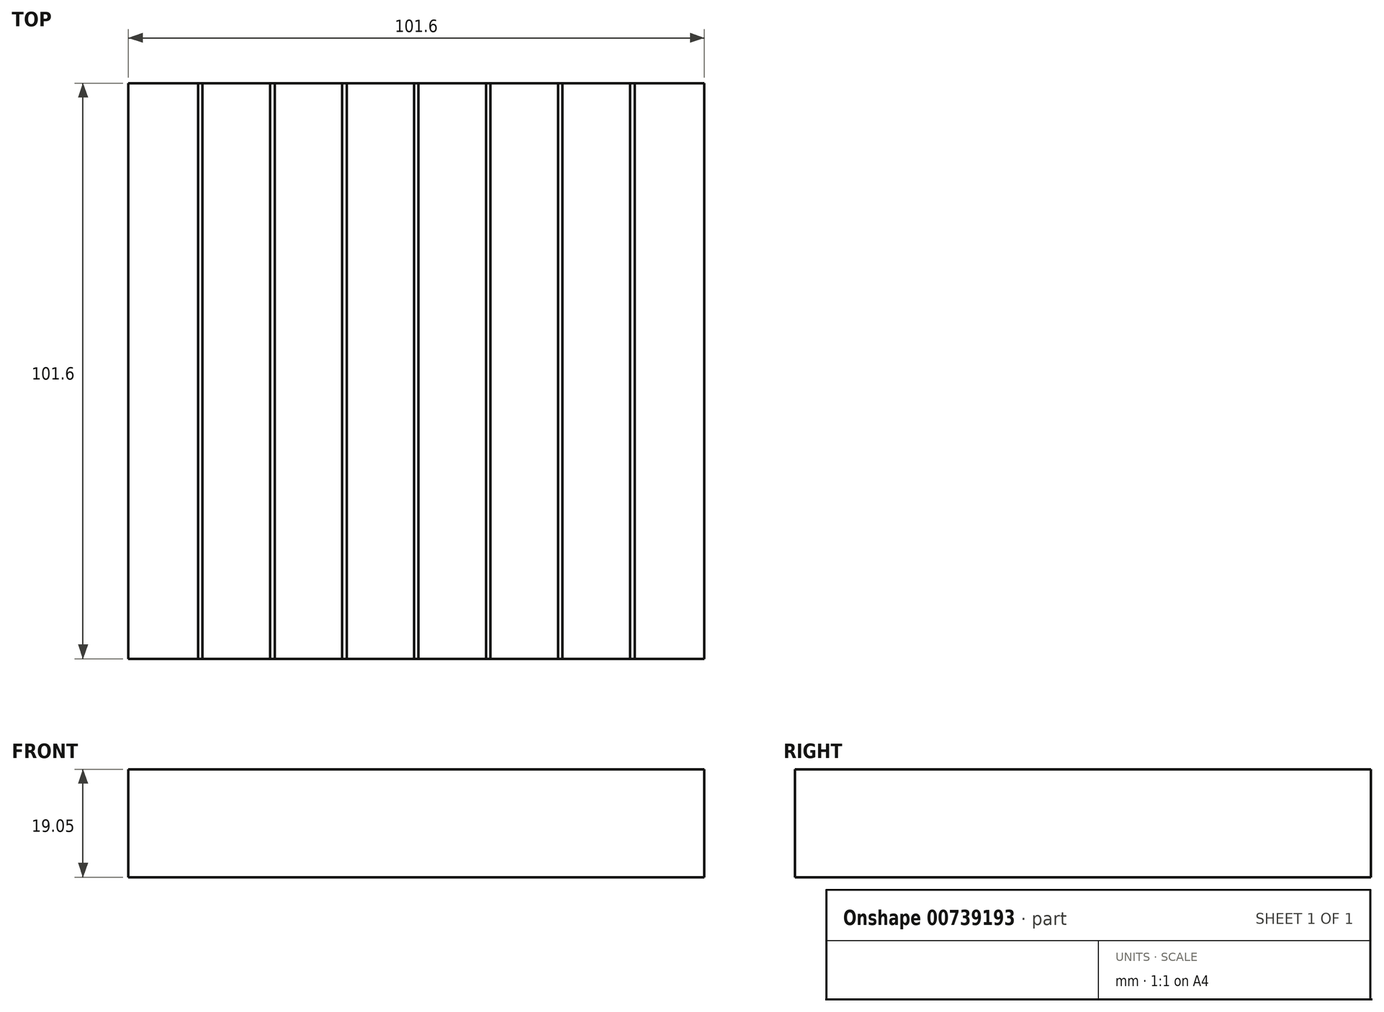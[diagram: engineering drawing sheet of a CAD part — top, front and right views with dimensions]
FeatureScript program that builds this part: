
annotation { "Feature Type Name" : "Feature", "Feature Type Description" : "" }
export const myFeature = defineFeature(function(context is Context, id is Id, definition is map)
    precondition{}
    {
        {
            var Q0;
            Q0=qCreatedBy(makeId("Top.planeOp"),FACE);
            var sketch = newSketch(context, id + "F0", { "sketchPlane" : qUnion([Q0])});
            skLineSegment(sketch, "E0.bottom", {"start": v(50.8, 50.8) * mm, "end": v(-50.8, 50.8) * mm});
            skLineSegment(sketch, "E0.top", {"start": v(50.8, -50.8) * mm, "end": v(-50.8, -50.8) * mm});
            skLineSegment(sketch, "E0.left", {"start": v(50.8, 50.8) * mm, "end": v(50.8, -50.8) * mm});
            skLineSegment(sketch, "E0.right", {"start": v(-50.8, 50.8) * mm, "end": v(-50.8, -50.8) * mm});
            skPoint(sketch, "E0.middle", {"position": v(0, 0) * mm});
            skSolve(sketch);
        }
        {
            var Q0;
            Q0=makeQuery(id+"F0.imprint","IMPRINT",FACE,{"disambiguationData":[TD([[makeQuery(id+"F0.imprint","IMPRINT",EDGE,{"derivedFrom":sQuery(id+"F0.wireOp",EDGE,"E0.bottom")}),1.0]])]});
            extrude(context, id + "F1", {"entities" : qUnion([Q0]), "depth" : 19.05 * mm, "offsetDistance" : 25.4 * mm});
        }
        {
            var Q0;
            Q0=makeQuery(id+"F1.opExtrude","CAP_FACE",FACE,{"disambiguationData":[OSD([sQuery(id+"F0.wireOp",EDGE,"E0.bottom"),sQuery(id+"F0.wireOp",EDGE,"E0.top"),sQuery(id+"F0.wireOp",EDGE,"E0.left"),sQuery(id+"F0.wireOp",EDGE,"E0.right")])],"isStart":false});
            var sketch = newSketch(context, id + "F2", { "sketchPlane" : qUnion([Q0])});
            skLineSegment(sketch, "E1", {"start": v(-38.5, 50.8) * mm, "end": v(-38.5, -50.8) * mm});
            skLineSegment(sketch, "E2", {"start": v(-38.1, -50.8) * mm, "end": v(-38.1, 50.8) * mm});
            skLineSegment(sketch, "E3", {"start": v(-37.7, 50.8) * mm, "end": v(-37.7, -50.8) * mm});
            skLineSegment(sketch, "E4.1.0.0", {"start": v(-25, 50.8) * mm, "end": v(-25, -50.8) * mm});
            skLineSegment(sketch, "E4.1.0.1", {"start": v(-25.8, 50.8) * mm, "end": v(-25.8, -50.8) * mm});
            skLineSegment(sketch, "E4.1.0.2", {"start": v(-25.4, -50.8) * mm, "end": v(-25.4, 50.8) * mm});
            skLineSegment(sketch, "E4.2.0.0", {"start": v(-12.3, 50.8) * mm, "end": v(-12.3, -50.8) * mm});
            skLineSegment(sketch, "E4.2.0.1", {"start": v(-13.1, 50.8) * mm, "end": v(-13.1, -50.8) * mm});
            skLineSegment(sketch, "E4.2.0.2", {"start": v(-12.7, -50.8) * mm, "end": v(-12.7, 50.8) * mm});
            skLineSegment(sketch, "E4.direction1", {"start": v(-38.5, -50.8) * mm, "end": v(-25.8, -50.8) * mm, "construction": true});
            skLineSegment(sketch, "E5.0.3.0", {"start": v(0.4, 50.8) * mm, "end": v(0.4, -50.8) * mm});
            skLineSegment(sketch, "E5.3.3.0", {"start": v(-0.4, 50.8) * mm, "end": v(-0.4, -50.8) * mm});
            skLineSegment(sketch, "E5.6.3.0", {"start": v(0, -50.8) * mm, "end": v(0, 50.8) * mm});
            skLineSegment(sketch, "E5.0.4.0", {"start": v(13.1, 50.8) * mm, "end": v(13.1, -50.8) * mm});
            skLineSegment(sketch, "E5.3.4.0", {"start": v(12.3, 50.8) * mm, "end": v(12.3, -50.8) * mm});
            skLineSegment(sketch, "E5.6.4.0", {"start": v(12.7, -50.8) * mm, "end": v(12.7, 50.8) * mm});
            skLineSegment(sketch, "E5.0.5.0", {"start": v(25.8, 50.8) * mm, "end": v(25.8, -50.8) * mm});
            skLineSegment(sketch, "E5.3.5.0", {"start": v(25, 50.8) * mm, "end": v(25, -50.8) * mm});
            skLineSegment(sketch, "E5.6.5.0", {"start": v(25.4, -50.8) * mm, "end": v(25.4, 50.8) * mm});
            skLineSegment(sketch, "E5.0.6.0", {"start": v(38.5, 50.8) * mm, "end": v(38.5, -50.8) * mm});
            skLineSegment(sketch, "E5.3.6.0", {"start": v(37.7, 50.8) * mm, "end": v(37.7, -50.8) * mm});
            skLineSegment(sketch, "E5.6.6.0", {"start": v(38.1, -50.8) * mm, "end": v(38.1, 50.8) * mm});
            skSolve(sketch);
        }
        {
            var Q0;
            {var subQ0=sQuery(id+"F2.wireOp",EDGE,"E1");Q0=makeQuery(id+"F2.imprint","IMPRINT",FACE,{"disambiguationData":[TD([[makeQuery(id+"F2.imprint","IMPRINT",EDGE,{"derivedFrom":subQ0}),1.0]])]});}
            var Q1;
            {var subQ0=sQuery(id+"F2.wireOp",EDGE,"E2");Q1=makeQuery(id+"F2.imprint","IMPRINT",FACE,{"disambiguationData":[TD([[makeQuery(id+"F2.imprint","IMPRINT",EDGE,{"derivedFrom":subQ0}),-1.0]])]});}
            var Q2;
            {var subQ0=sQuery(id+"F2.wireOp",EDGE,"E4.1.0.1");Q2=makeQuery(id+"F2.imprint","IMPRINT",FACE,{"disambiguationData":[TD([[makeQuery(id+"F2.imprint","IMPRINT",EDGE,{"derivedFrom":subQ0}),1.0]])]});}
            var Q3;
            {var subQ0=sQuery(id+"F2.wireOp",EDGE,"E4.1.0.0");Q3=makeQuery(id+"F2.imprint","IMPRINT",FACE,{"disambiguationData":[TD([[makeQuery(id+"F2.imprint","IMPRINT",EDGE,{"derivedFrom":subQ0}),-1.0]])]});}
            var Q4;
            {var subQ0=sQuery(id+"F2.wireOp",EDGE,"E4.2.0.1");Q4=makeQuery(id+"F2.imprint","IMPRINT",FACE,{"disambiguationData":[TD([[makeQuery(id+"F2.imprint","IMPRINT",EDGE,{"derivedFrom":subQ0}),1.0]])]});}
            var Q5;
            {var subQ0=sQuery(id+"F2.wireOp",EDGE,"E4.2.0.0");Q5=makeQuery(id+"F2.imprint","IMPRINT",FACE,{"disambiguationData":[TD([[makeQuery(id+"F2.imprint","IMPRINT",EDGE,{"derivedFrom":subQ0}),-1.0]])]});}
            var Q6;
            {var subQ0=sQuery(id+"F2.wireOp",EDGE,"E5.3.3.0");Q6=makeQuery(id+"F2.imprint","IMPRINT",FACE,{"disambiguationData":[TD([[makeQuery(id+"F2.imprint","IMPRINT",EDGE,{"derivedFrom":subQ0}),1.0]])]});}
            var Q7;
            {var subQ0=sQuery(id+"F2.wireOp",EDGE,"E5.0.3.0");Q7=makeQuery(id+"F2.imprint","IMPRINT",FACE,{"disambiguationData":[TD([[makeQuery(id+"F2.imprint","IMPRINT",EDGE,{"derivedFrom":subQ0}),-1.0]])]});}
            var Q8;
            {var subQ0=sQuery(id+"F2.wireOp",EDGE,"E5.3.4.0");Q8=makeQuery(id+"F2.imprint","IMPRINT",FACE,{"disambiguationData":[TD([[makeQuery(id+"F2.imprint","IMPRINT",EDGE,{"derivedFrom":subQ0}),1.0]])]});}
            var Q9;
            {var subQ0=sQuery(id+"F2.wireOp",EDGE,"E5.0.4.0");Q9=makeQuery(id+"F2.imprint","IMPRINT",FACE,{"disambiguationData":[TD([[makeQuery(id+"F2.imprint","IMPRINT",EDGE,{"derivedFrom":subQ0}),-1.0]])]});}
            var Q10;
            {var subQ0=sQuery(id+"F2.wireOp",EDGE,"E5.3.5.0");Q10=makeQuery(id+"F2.imprint","IMPRINT",FACE,{"disambiguationData":[TD([[makeQuery(id+"F2.imprint","IMPRINT",EDGE,{"derivedFrom":subQ0}),1.0]])]});}
            var Q11;
            {var subQ0=sQuery(id+"F2.wireOp",EDGE,"E5.0.5.0");Q11=makeQuery(id+"F2.imprint","IMPRINT",FACE,{"disambiguationData":[TD([[makeQuery(id+"F2.imprint","IMPRINT",EDGE,{"derivedFrom":subQ0}),-1.0]])]});}
            var Q12;
            {var subQ0=sQuery(id+"F2.wireOp",EDGE,"E5.3.6.0");Q12=makeQuery(id+"F2.imprint","IMPRINT",FACE,{"disambiguationData":[TD([[makeQuery(id+"F2.imprint","IMPRINT",EDGE,{"derivedFrom":subQ0}),1.0]])]});}
            var Q13;
            {var subQ0=sQuery(id+"F2.wireOp",EDGE,"E5.0.6.0");Q13=makeQuery(id+"F2.imprint","IMPRINT",FACE,{"disambiguationData":[TD([[makeQuery(id+"F2.imprint","IMPRINT",EDGE,{"derivedFrom":subQ0}),-1.0]])]});}
            extrude(context, id + "F3", {"entities" : qUnion([Q0, Q1, Q2, Q3, Q4, Q5, Q6, Q7, Q8, Q9, Q10, Q11, Q12, Q13]), "operationType" : NewBodyOperationType.REMOVE, "oppositeDirection" : true, "depth" : 1 / 406.4 * mm, "offsetDistance" : 25.4 * mm});
        }
    });
